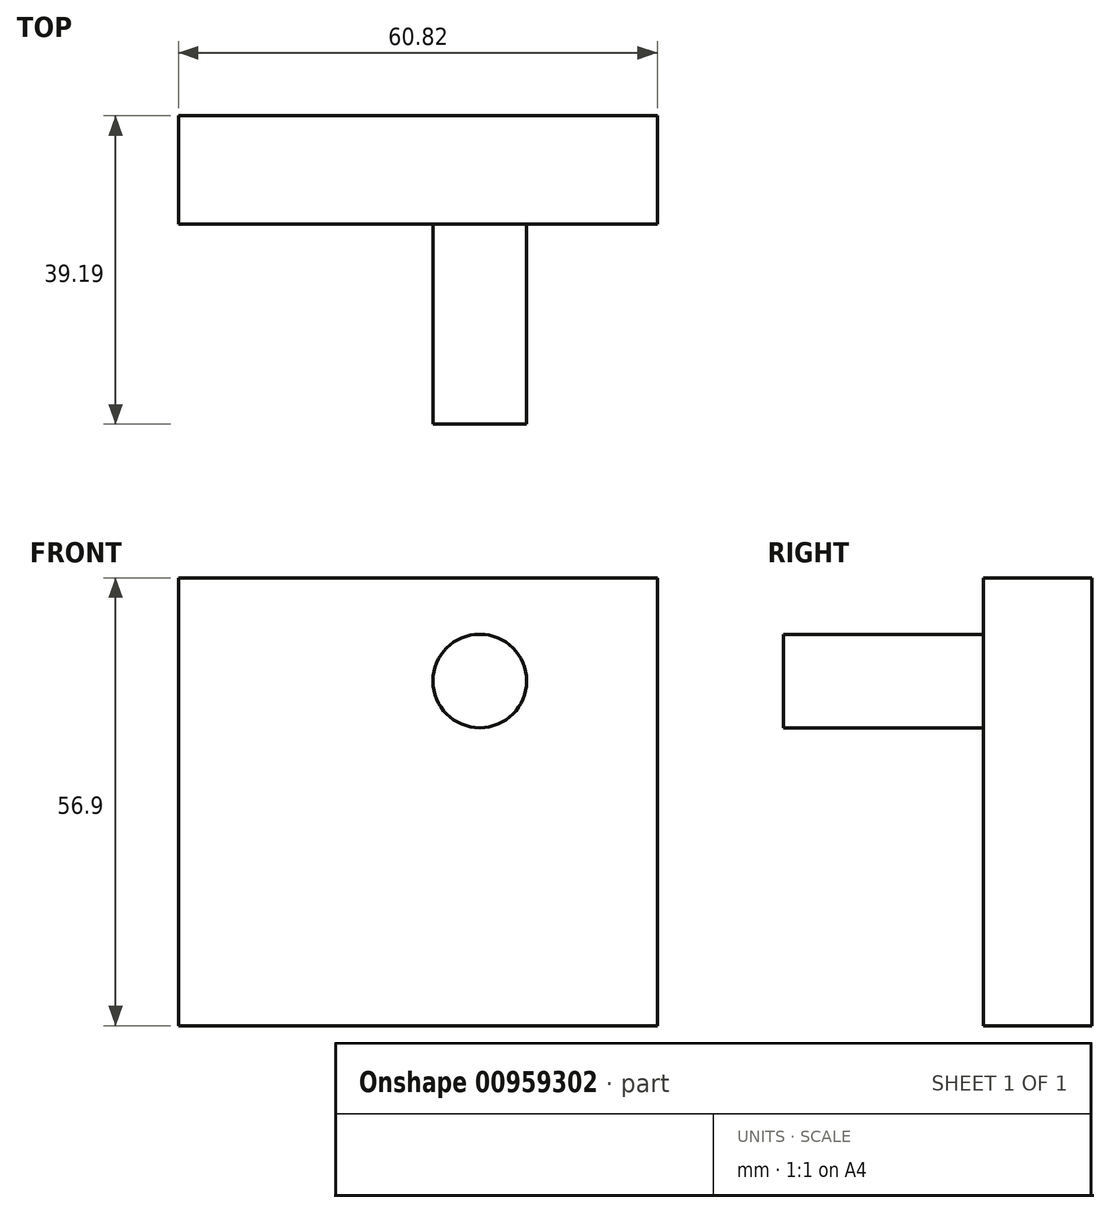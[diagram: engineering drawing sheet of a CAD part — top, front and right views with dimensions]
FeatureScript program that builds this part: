
annotation { "Feature Type Name" : "Feature", "Feature Type Description" : "" }
export const myFeature = defineFeature(function(context is Context, id is Id, definition is map)
    precondition{}
    {
        {
            var Q0;
            Q0=qCreatedBy(makeId("Top.planeOp"),FACE);
            var sketch = newSketch(context, id + "F0", { "sketchPlane" : qUnion([Q0])});
            skLineSegment(sketch, "E0.bottom", {"start": v(-9.68, 5.66) * mm, "end": v(51.14, 5.66) * mm});
            skLineSegment(sketch, "E0.top", {"start": v(-9.68, -33.53) * mm, "end": v(51.14, -33.53) * mm});
            skLineSegment(sketch, "E0.left", {"start": v(-9.68, 5.66) * mm, "end": v(-9.68, -33.53) * mm});
            skLineSegment(sketch, "E0.right", {"start": v(51.14, 5.66) * mm, "end": v(51.14, -33.53) * mm});
            skSolve(sketch);
        }
        {
            var Q0;
            Q0 = qSketchRegion(id + "F0", true);
            extrude(context, id + "F1", {"entities" : qUnion([Q0]), "depth" : 56.9 * mm, "offsetDistance" : 25.4 * mm});
        }
        {
            var Q0;
            Q0=makeQuery(id+"F1.opExtrude","SWEPT_FACE",FACE,{"disambiguationData":[OSD([sQuery(id+"F0.wireOp",EDGE,"E0.top")])]});
            var sketch = newSketch(context, id + "F2", { "sketchPlane" : qUnion([Q0])});
            skCircle(sketch, "E1", {"center": v(9.11, 42.65) * mm, "radius": 5.67 * mm});
            skCircle(sketch, "E2", {"center": v(28.6, 43.79) * mm, "radius": 5.94 * mm});
            skCircle(sketch, "E3", {"center": v(21.22, 26.39) * mm, "radius": 6.56 * mm});
            skSolve(sketch);
        }
        {
            var Q0;
            Q0=makeQuery(id+"F2.imprint","IMPRINT",FACE,{"disambiguationData":[TD([[makeQuery(id+"F2.imprint","IMPRINT",EDGE,{"derivedFrom":sQuery(id+"F2.wireOp",EDGE,"E1")}),1.0]])]});
            var Q1;
            Q1=makeQuery(id+"F2.imprint","IMPRINT",FACE,{"disambiguationData":[TD([[makeQuery(id+"F2.imprint","IMPRINT",EDGE,{"derivedFrom":sQuery(id+"F2.wireOp",EDGE,"E3")}),1.0]])]});
            var Q2;
            Q2=makeQuery(id+"F2.imprint","IMPRINT",FACE,{"disambiguationData":[TD([[makeQuery(id+"F2.imprint","IMPRINT",EDGE,{"derivedFrom":sQuery(id+"F2.wireOp",EDGE,"E1")}),-1.0]])]});
            extrude(context, id + "F3", {"entities" : qUnion([Q0, Q1, Q2]), "operationType" : NewBodyOperationType.REMOVE, "oppositeDirection" : true, "depth" : 25.4 * mm, "offsetDistance" : 25.4 * mm});
        }
    });
